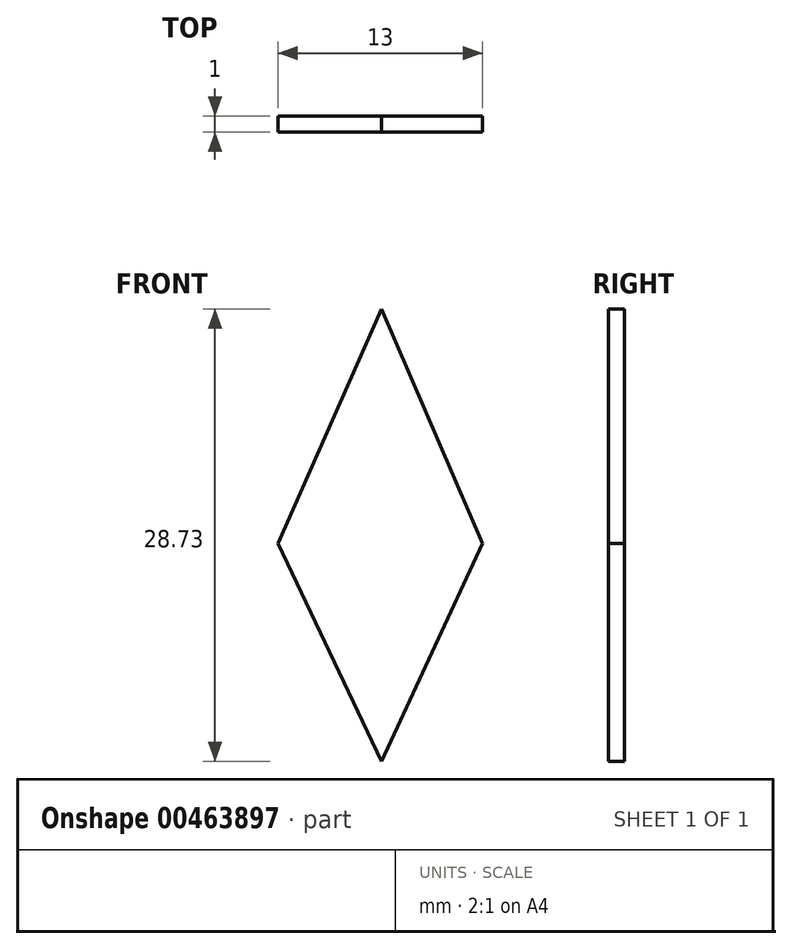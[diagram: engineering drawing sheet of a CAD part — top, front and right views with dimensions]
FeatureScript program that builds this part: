
annotation { "Feature Type Name" : "Feature", "Feature Type Description" : "" }
export const myFeature = defineFeature(function(context is Context, id is Id, definition is map)
    precondition{}
    {
        {
            var Q0;
            Q0=qCreatedBy(makeId("Front.planeOp"),FACE);
            var sketch = newSketch(context, id + "F0", { "sketchPlane" : qUnion([Q0])});
            skLineSegment(sketch, "E0", {"start": v(0, 0) * mm, "end": v(6.4, 13.85) * mm});
            skLineSegment(sketch, "E1", {"start": v(6.4, 13.85) * mm, "end": v(-6.6, 13.85) * mm});
            skLineSegment(sketch, "E2", {"start": v(-6.6, 13.85) * mm, "end": v(0, 0) * mm});
            skLineSegment(sketch, "E3", {"start": v(-6.6, 13.85) * mm, "end": v(0, 28.73) * mm});
            skLineSegment(sketch, "E4", {"start": v(0, 28.73) * mm, "end": v(6.4, 13.85) * mm});
            skSolve(sketch);
        }
        {
            var Q0;
            Q0 = qSketchRegion(id + "F0", true);
            extrude(context, id + "F1", {"entities" : qUnion([Q0]), "depth" : 1 * mm});
        }
    });
